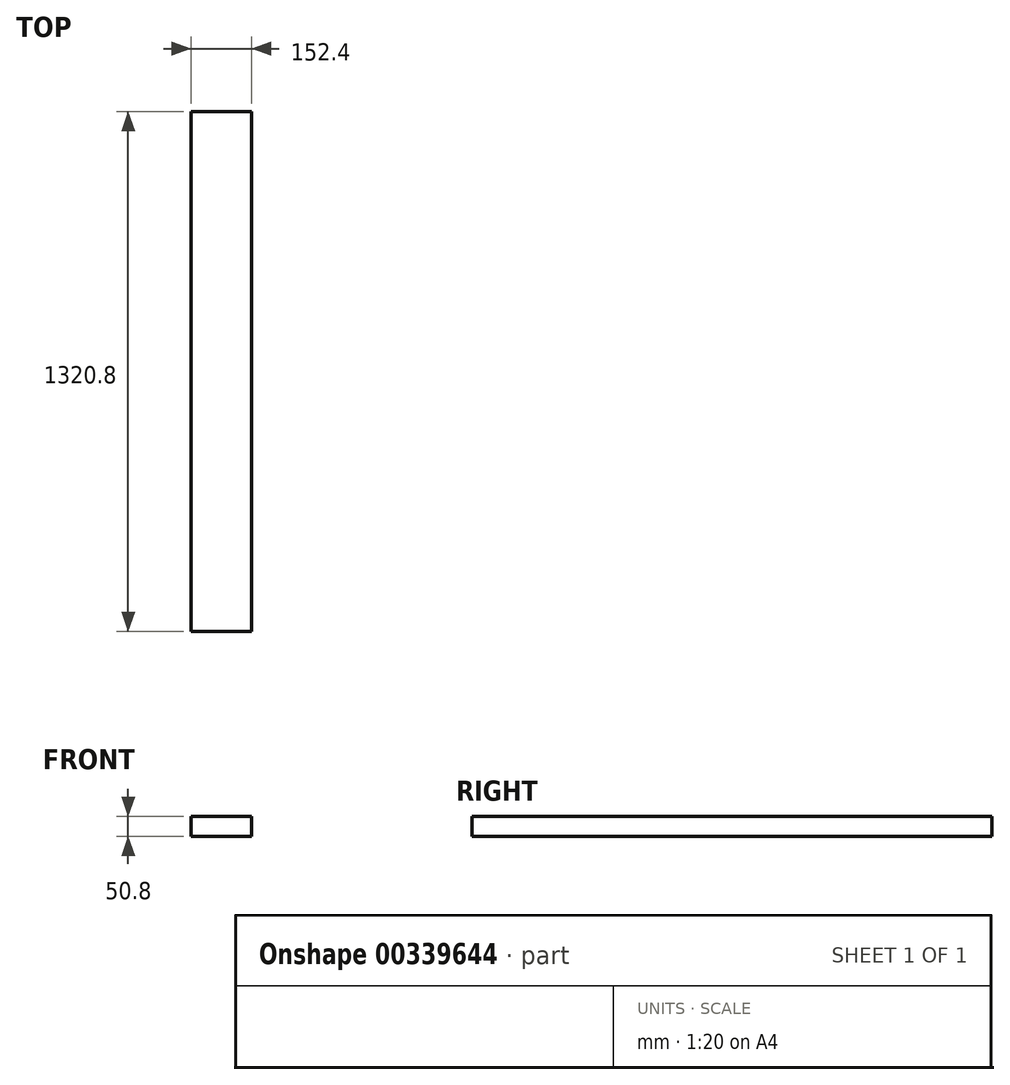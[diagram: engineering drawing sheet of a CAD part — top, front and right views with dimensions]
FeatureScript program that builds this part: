
annotation { "Feature Type Name" : "Feature", "Feature Type Description" : "" }
export const myFeature = defineFeature(function(context is Context, id is Id, definition is map)
    precondition{}
    {
        {
            var Q0;
            Q0=qCreatedBy(makeId("Front.planeOp"),FACE);
            var sketch = newSketch(context, id + "F0", { "sketchPlane" : qUnion([Q0])});
            skLineSegment(sketch, "E0.bottom", {"start": v(-76.2, 25.4) * mm, "end": v(76.2, 25.4) * mm});
            skLineSegment(sketch, "E0.top", {"start": v(-76.2, -25.4) * mm, "end": v(76.2, -25.4) * mm});
            skLineSegment(sketch, "E0.left", {"start": v(-76.2, 25.4) * mm, "end": v(-76.2, -25.4) * mm});
            skLineSegment(sketch, "E0.right", {"start": v(76.2, 25.4) * mm, "end": v(76.2, -25.4) * mm});
            skPoint(sketch, "E0.middle", {"position": v(0, 0) * mm});
            skSolve(sketch);
        }
        {
            var Q0;
            Q0=makeQuery(id+"F0.imprint","IMPRINT",FACE,{"disambiguationData":[TD([[makeQuery(id+"F0.imprint","IMPRINT",EDGE,{"derivedFrom":sQuery(id+"F0.wireOp",EDGE,"E0.bottom")}),-1.0]])]});
            extrude(context, id + "F1", {"entities" : qUnion([Q0]), "endBound" : BoundingType.SYMMETRIC, "depth" : 1320.8 * mm});
        }
    });
